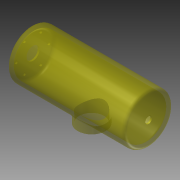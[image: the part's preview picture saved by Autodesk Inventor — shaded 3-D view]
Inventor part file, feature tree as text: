
AUTODESK INVENTOR PART (.ipt)
format: ipt  version: 2015 (Build 190159000, 159)  size: 254,464 bytes
history: native  units: mm
features: extrude x9, sketch x8, fillet x5, projected_geometry x3, plane x1
ambient origin geometry x8: Origin, YZ Plane, XZ Plane, XY Plane, X Axis, Y Axis, Z Axis, Center Point
bodies: Solid1 (feature_tree)
feature tree (26):
  extrude  "Extrusion1"  Depth=71.7mm TaperAngle=0.0deg
  plane  "Work Plane1"
  sketch  "Sketch2"  dims[d3=34.82mm d4=17.15mm]
  extrude  "Extrusion2"  Depth=17.15mm
  sketch  "Sketch9"  dims[d5=71.7mm d6=0.0mm d31=2.0mm d32=70.7mm d33=0.0mm d34=2.0mm]
  extrude  "Extrusion11"  Depth=2.0mm
  fillet  "Fillet3"  Radius=70.7mm
  fillet  "Fillet4"  Radius=2.0mm
  extrude  "Extrusion12"  Depth=1.0mm TaperAngle=0.0deg
  fillet  "Fillet6"  Radius=2.0mm
  fillet  "Fillet7"  Radius=2.0mm
  extrude  "Extrusion13"  Depth=4.064mm
  fillet  "Fillet8"  Radius=12.7mm
  extrude  "Extrusion15"  Depth=1.0mm
  extrude  "Extrusion16"  Depth=4.0mm TaperAngle=0.0deg
  extrude  "Extrusion17"  Depth=10.0mm
  extrude  "Extrusion18"  Depth=10.0mm
  sketch  "Sketch1"  dims[d0=29.85mm d1=71.7mm d2=0.0mm]
  projected_geometry  "Projected Loop1"
  sketch  "Sketch10"  dims[d35=2.0mm d37=1.0mm d38=0.0mm d39=2.0mm d40=2.0mm]
  projected_geometry  "Projected Loop5"
  sketch  "Sketch11"  dims[d42=11.1mm d43=4.064mm d44=12.7mm d45=0.0mm]
  sketch  "Sketch12"  dims[d48=2.0mm d49=1.0mm]
  projected_geometry  "Projected Loop6"
  sketch  "Sketch13"  dims[d50=2.0mm d51=0.0mm d52=4.0mm d53=0.0mm]
  sketch  "Sketch14"  dims[d54=20.0mm d55=3.0mm d56=1.5mm d57=60.0mm d59=360.0deg d61=4.0mm d62=0.0mm d63=8.0mm d64=10.0mm d65=0.0mm d66=1.03mm]
